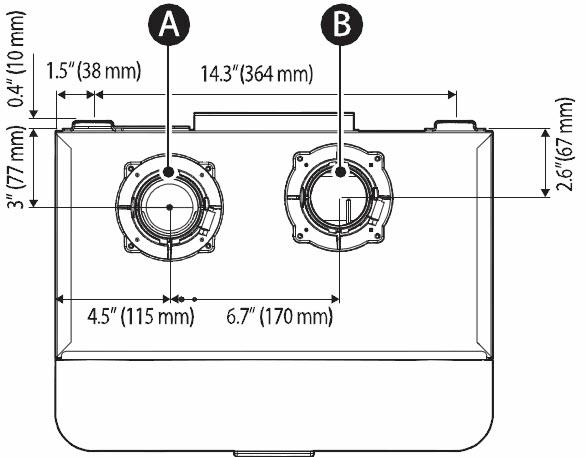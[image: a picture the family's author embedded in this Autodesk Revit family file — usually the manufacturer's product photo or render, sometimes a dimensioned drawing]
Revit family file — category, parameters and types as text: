
# Revit family: Water_Heater-Navien-NPE_S_Series
name_source: partatom
category: Mechanical Equipment
revit_build: Autodesk Revit MEP 2013 (Build: 20130531_2115(x64)
units: mm (PartAtom-declared; Revit-internal decimal feet)

## types (3) — shared parameters
Apparent Load = 0 VA
Cold Water Inlet = 1"
Default Elevation = 4' - 0"
Description = Premium Condensing Tankless Gas Water Heater (NPE-S)
Exhaust = 3"
Finish = Metal - Navien - White
Frequency = 60 Hz
Gas Inlet = 1"
Height = 2' - 3 13/32"
Hot Water Outlet = 1"
Intake = 3"
Length = 1' - 1 3/16"
Manufacturer = Navien
Natural Gas Supply Pressure = 3.5 inches - 10.5 inches
Number of Poles = 1
Phase = 1
Power Factor = 1
Product Documentation Link = http://us.navien.com
Product Name = NPE-S
Product Page URL = http://us.navien.com
Propane Gas Supply Pressure = 8.0 inches - 13.0 inches
Recirculation Inlet = 1"
URL = http://us.navien.com
Voltage = 120 V
Water Pressure = 15-150 PSI
Width = 1' - 5 5/16"

## per-type parameters (varying)
| type | Flow Rate | Heating Capacity | Model | Operating Weight |
| NPE 180S | 6.5 GPM | 150000.0 Btu/h | NPE-180S | 67.00 lb |
| NPE 210S | 10.1 GPM | 180000.0 Btu/h | NPE-210S | 75.00 lb |
| NPE 240S | 11.2 GPM | 199900.0 Btu/h | NPE-240S | 75.00 lb |

## geometry (parser evidence)
native form markers: Blend x4, Sweep x4
no freeform markers — native parametric forms only
